# Revit family: Grab-Bar_Contemporary_Soiree_YG96024_TOTO
name_source: partatom
category: Furniture
revit_build: Autodesk Revit Architecture 2013 (Build: 20130531_2115(x64)
units: mm (PartAtom-declared; Revit-internal decimal feet)

## types (1)
- YG97024
    04 CSI = 10 28 00
    95 CSI = 10800
    ADA Compliant = Yes
    Assembly Code = C1030200
    CAD Drawing URL = http://assets.totousa.com
    Color Availability = #CP  Polished Chrome
    Default Elevation = 3' - 0"
    Depth = 0' - 2 3/4"
    Description = Grab Bar
    Finish = Metal - TOTO - Chrome - Polished
    Height = 0' - 2 13/16"
    Manufacturer = TOTO USA, Inc.
    Manufacturer Fax = (770) 282-0002
    Model = YG96024
    Series = Soiree
    Shipping Weight = 4.70 lb
    Spec Sheet URL = http://assets.totousa.com
    Style = Contemporary
    Subcategory = Accessories
    Toto BIM Number = BM-00140
    Toto Version = V.02
    URL = http://www.totousa.com
    Warranty = Lifetime Limited Warranty (Residential Use), One Year Limited (Commercial Use)
    Warranty URL = http://www.totousa.com
    Width = 2' - 5 1/8"

## geometry (parser evidence)
native form markers: Blend x6, Sweep x1
no freeform markers — native parametric forms only
